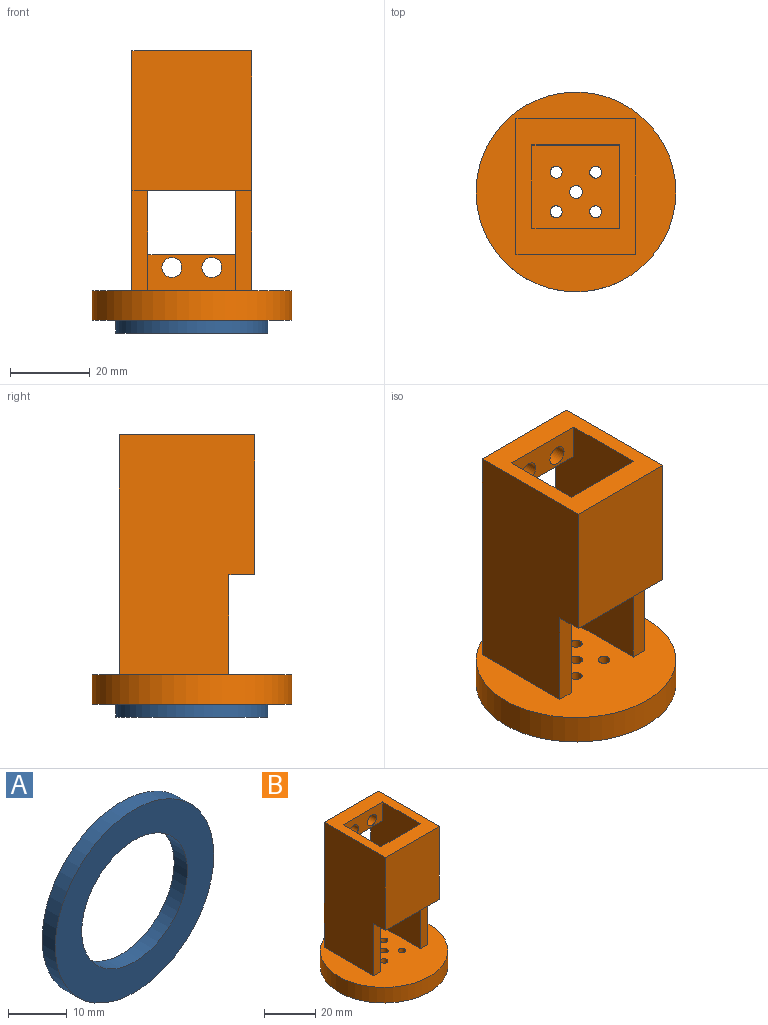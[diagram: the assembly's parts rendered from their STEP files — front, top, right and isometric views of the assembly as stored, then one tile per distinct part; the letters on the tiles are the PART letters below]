
ASSEMBLY  parts=2 mates=1
PART A: 4 faces, bbox 38.1x3.2x38.1 mm
  f0: plane 38.1x38.1mm, normal (0,-1,0), area 633.4mm2, adj f2,f3
  f1: plane 38.1x38.1mm, normal (0,1,0), area 633.4mm2, adj f2,f3
  f2: cylinder r=19.05mm len=38.1mm, axis (0,1,0), area 380mm2, adj f0,f1
  f3: cylinder r=12.7mm len=25.4mm, axis (0,1,0), area 253.4mm2, adj f0,f1
PART B: 29 faces, bbox 50x50x70.5 mm
  f0: plane 22x9mm, normal (0,-1,0), area 158.7mm2, adj f15,f16,f19,f20,f21,f22
  f1: plane 22x9mm, normal (0,-1,0), area 158.7mm2, adj f3,f17,f18,f21,f22,f23
  f2: plane 60x30mm, normal (0,1,0), area 797.5mm2, adj f3,f13,f14,f15,f16,f17,f18,f19
  f3: plane 50x50mm, normal (0,0,1), area 1564.2mm2, adj f1,f2,f4,f8,f9,f10,f11,f12
  f4: cylinder r=25mm len=50mm, axis (0,0,-1), area 1178.1mm2, adj f3,f5
  f5: plane 50x50mm, normal (0,0,-1), area 1456.8mm2, adj f4,f6
  f6: cylinder r=12.7mm len=25.4mm, axis (0,0,1), area 239.4mm2, adj f5,f7
  f7: plane 25.4x25.4mm, normal (0,0,-1), area 470.4mm2, adj f6,f8,f9,f10,f11,f12
  f8: cylinder r=1.6mm len=10.5mm, axis (0,0,1), area 105.6mm2, adj f3,f7
  f9: cylinder r=1.5mm len=10.5mm, axis (0,0,1), area 99mm2, adj f3,f7
  f10: cylinder r=1.5mm len=10.5mm, axis (0,0,1), area 99mm2, adj f3,f7
  f11: cylinder r=1.5mm len=10.5mm, axis (0,0,1), area 99mm2, adj f3,f7
  f12: cylinder r=1.5mm len=10.5mm, axis (0,0,1), area 99mm2, adj f3,f7
  f13: plane 60x34mm, normal (1,0,0), area 1877.5mm2, adj f2,f3,f15,f24,f27,f28
  f14: plane 60x34mm, normal (-1,0,0), area 1877.5mm2, adj f2,f3,f15,f25,f27,f28
  f15: plane 34x30mm, normal (0,0,1), area 558mm2, adj f0,f2,f13,f14,f21,f22,f26,f28
  f16: cylinder r=2.5mm len=6.5mm, axis (0,-1,0), area 102.1mm2, adj f0,f2
  f17: cylinder r=2.5mm len=6.5mm, axis (0,-1,0), area 102.1mm2, adj f1,f2
  f18: cylinder r=2.5mm len=6.5mm, axis (0,-1,0), area 102.1mm2, adj f1,f2
  f19: cylinder r=2.5mm len=6.5mm, axis (0,-1,0), area 102.1mm2, adj f0,f2
  f20: plane 22x6.5mm, normal (0,0,-1), area 143mm2, adj f0,f2,f21,f22
  f21: plane 60x27.5mm, normal (-1,0,0), area 1533mm2, adj f0,f1,f2,f3,f15,f20,f23,f24
  f22: plane 60x27.5mm, normal (1,0,0), area 1533mm2, adj f0,f1,f2,f3,f15,f20,f23,f25
  f23: plane 22x6.5mm, normal (0,0,1), area 143mm2, adj f1,f2,f21,f22
  f24: plane 25x4mm, normal (0,-1,0), area 100mm2, adj f3,f13,f21,f27
  f25: plane 25x4mm, normal (0,-1,0), area 100mm2, adj f3,f14,f22,f27
  f26: plane 35x22mm, normal (0,1,0), area 770mm2, adj f15,f21,f22,f27
  f27: plane 30x6.5mm, normal (0,0,-1), area 195mm2, adj f13,f14,f24,f25,f26,f28
  f28: plane 35x30mm, normal (0,-1,0), area 1050mm2, adj f13,f14,f15,f27
PLACE A rot(axis=(-0.58,-0.58,0.58),120deg) t=(-16.61,-8.15,-1.33)mm
PLACE B t=(-16.61,-8.15,0.26)mm fixed
MATE fastened B.f4 <-> A.f2  axis (0,0,-1) through (-16.61,-8.15,0.26)mm
